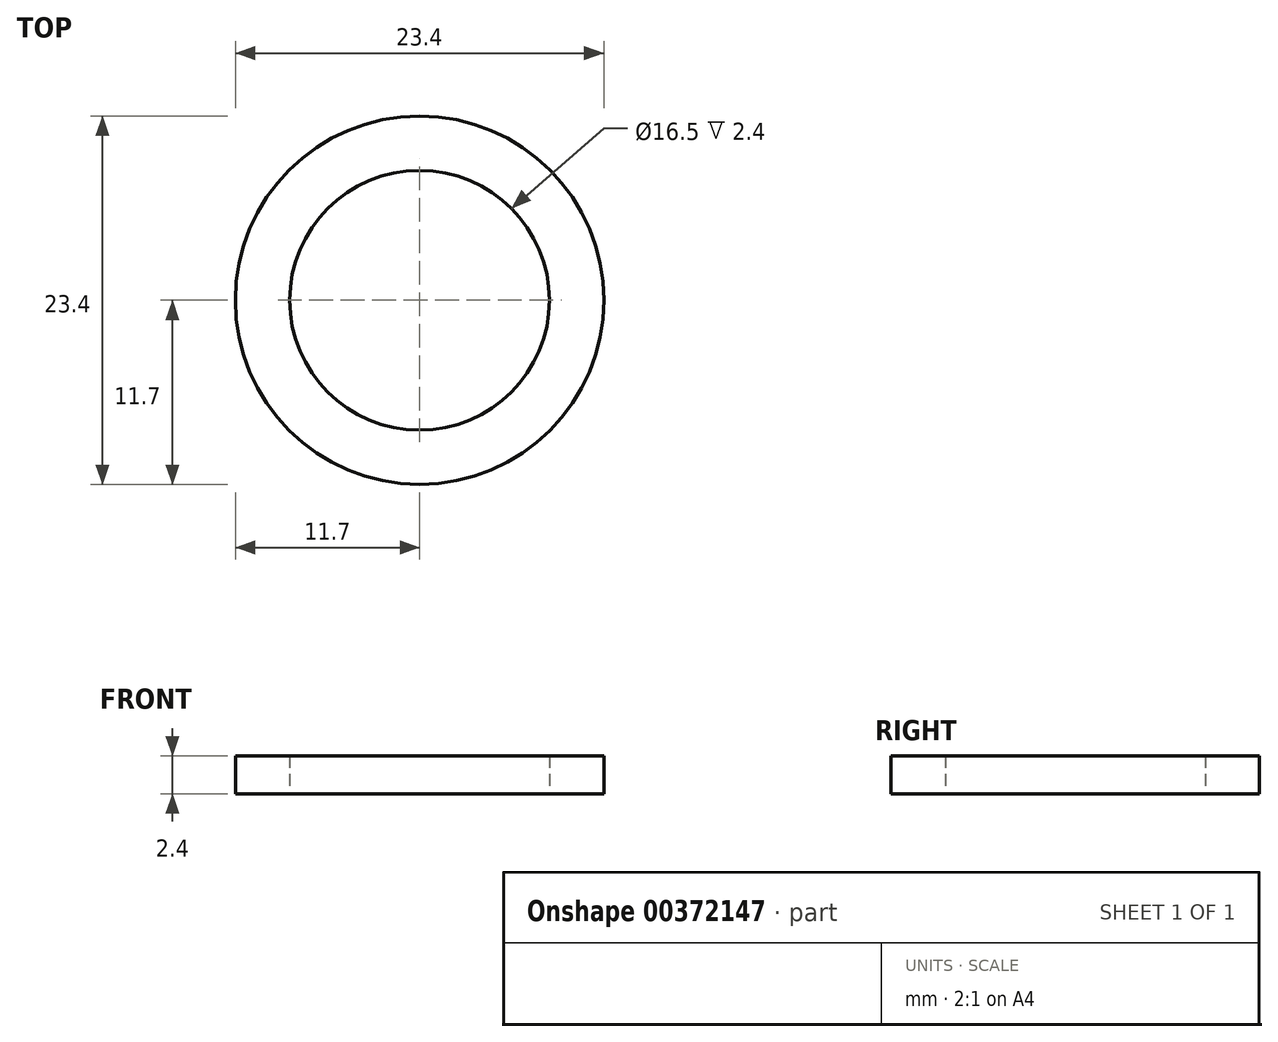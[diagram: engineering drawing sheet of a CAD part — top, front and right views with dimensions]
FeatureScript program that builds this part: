
annotation { "Feature Type Name" : "Feature", "Feature Type Description" : "" }
export const myFeature = defineFeature(function(context is Context, id is Id, definition is map)
    precondition{}
    {
        {
            var Q0;
            Q0=qCreatedBy(makeId("Top.planeOp"),FACE);
            var sketch = newSketch(context, id + "F0", { "sketchPlane" : qUnion([Q0])});
            skCircle(sketch, "E0", {"center": v(0, 0) * mm, "radius": 2.75 * mm});
            skCircle(sketch, "E1", {"center": v(0, 0) * mm, "radius": 3.9 * mm});
            skSolve(sketch);
        }
        {
            var Q0;
            Q0=makeQuery(id+"F0.imprint","IMPRINT",FACE,{"disambiguationData":[TD([[makeQuery(id+"F0.imprint","IMPRINT",EDGE,{"derivedFrom":sQuery(id+"F0.wireOp",EDGE,"E0")}),-1.0]])]});
            extrude(context, id + "F1", {"entities" : qUnion([Q0]), "depth" : 0.8 * mm});
        }
        {
            var Q0;
            Q0=makeQuery(id+"F1.opExtrude","SWEPT_BODY",BODY,{"disambiguationData":[OSD([sQuery(id+"F0.wireOp",EDGE,"E0"),sQuery(id+"F0.wireOp",EDGE,"E1")])]});
            var Q1;
            Q1=qCreatedBy(makeId("Origin.pointOp"),VERTEX);
            transform(context, id + "F2", {"entities" : qUnion([Q0]), "transformType" : TransformType.SCALE_UNIFORMLY, "scale" : 3, "makeCopy" : false, "scalePoint" : qUnion([Q1])});
        }
    });
